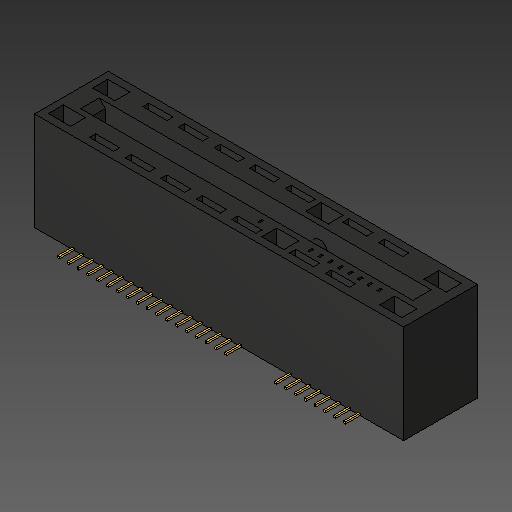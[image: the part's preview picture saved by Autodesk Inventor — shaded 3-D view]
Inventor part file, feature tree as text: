
AUTODESK INVENTOR PART (.ipt)
format: ipt  version: 2018.2 (Build 222227000, 227)  size: 313,856 bytes
history: native  units: mm
features: other x1, chamfer x1
ambient origin geometry x8: Origin, YZ Plane, XZ Plane, XY Plane, X Axis, Y Axis, Z Axis, Center Point
bodies: Body1 (feature_tree)
feature tree (2):
  other  "ソリッド1"
  chamfer  "Chamfer1"  [1 undecoded]
note: 1 required parameter value undecoded (feature->parameter linkage not recoverable at this tier; creation-order binding heuristic only, values carry confidence <= 0.55)
